# Revit family: Mixing_Valve-HL-Bradley_Corp-High_Capacity_2x1-S59-3260
name_source: partatom
category: Pipe Accessories
revit_build: Autodesk Revit MEP 2012 (Build: 20110309_2315(x64)
units: mm (PartAtom-declared; Revit-internal decimal feet)

## types (1)
- HL 2x1 High Capacity
    ADA Compliant = No
    Assembly Code = D2090800
    Description = High Capacity Manifold System
    Industry Standards = ASSE 1017, UPC & CSA. Certified by IAPMO to meet the lead-free requirements of CA AB 1953.
    Manufacturer = Bradley Corporation
    MasterFormat Number = 22 40 00
    MasterFormat Title = Plumbing Fixture
    Material = Lead-free Brass
    Maximum Inlet Temperature = 200° F (93° C)
    Maximum Operating Pressure = 125.00 psi
    Minimum Flow = 8 GPM
    Model = S59-3260
    Modeling Code = ABO090703ACP1600ABC090703TAS1707
    NPT = 2"
    NPT Radius = 1"
    Nut Material = Metal - Bradley Corp - Light Bronze
    OmniClass Code = 23.65.55.14.24
    OmniClass Title = Mixing Valves for Liquid Services
    Product Tech Data URL - English = http://bradleycorp.com
    Set Point = 110°F (43°C)
    Set Point Notes = "Refer to Bradley Technical Data for other set point ranges."
    Specifications URL = http://www.bradleycorp.com
    Temperature Notes = "Refer to Bradley Technical Data for other temperature ranges."
    Temperature Range = Std. 90°F (32°C) to 120°F (49°C)
    URL = http://www.bradleycorp.com
    Valve Material = Metal - Bradley Corp - Bronze
    Valve Type = Bradley - S59 - For Nesting : HL130
    Version = 2.0

## geometry (parser evidence)
native form markers: Blend x9, Sweep x4
no freeform markers — native parametric forms only
